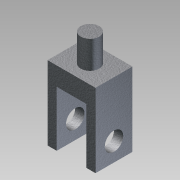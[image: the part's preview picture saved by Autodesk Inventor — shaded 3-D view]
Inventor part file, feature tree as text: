
AUTODESK INVENTOR PART (.ipt)
format: ipt  version: 2012 (Build 160160000, 160)  size: 112,640 bytes
history: native  units: in
note: dims shown in document units (in); Inventor stores cm internally (conversion verified against a paired STEP export)
features: extrude x3, sketch x3
ambient origin geometry x8: Origin, YZ Plane, XZ Plane, XY Plane, X Axis, Y Axis, Z Axis, Center Point
bodies: Solid1 (feature_tree)
feature tree (6):
  extrude  "Extrusion1"  Depth=2.0in
  extrude  "Extrusion2"  Depth=0.25in
  extrude  "Extrusion3"  Depth=1.0in TaperAngle=0.0deg
  sketch  "Sketch1"  dims[d0=1.3in d1=2.0in]
  sketch  "Sketch2"  dims[d2=0.25in d3=0.25in]
  sketch  "Sketch3"  dims[d4=0.25in d5=1.0in d6=0.0in d7=0.5in d8=0.5in d9=10.0in d10=0.0in d11=2.0in d12=0.5in d13=0.75in d14=0.0in d15=1.5in]
